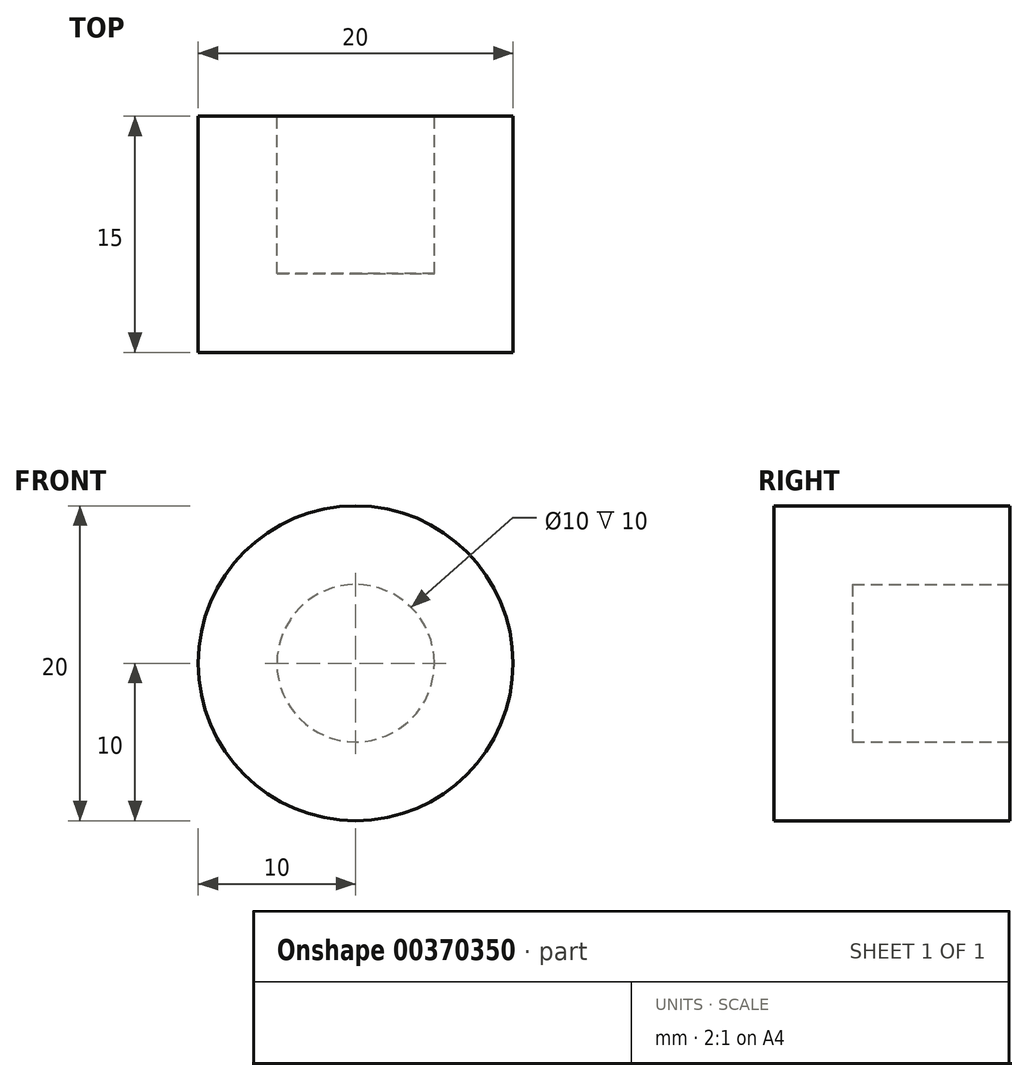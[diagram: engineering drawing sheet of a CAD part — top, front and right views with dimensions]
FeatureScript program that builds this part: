
annotation { "Feature Type Name" : "Feature", "Feature Type Description" : "" }
export const myFeature = defineFeature(function(context is Context, id is Id, definition is map)
    precondition{}
    {
        {
            var Q0;
            Q0=qCreatedBy(makeId("Right.planeOp"),FACE);
            var sketch = newSketch(context, id + "F0", { "sketchPlane" : qUnion([Q0])});
            skLineSegment(sketch, "E0", {"start": v(-10, 5) * mm, "end": v(-20, 5) * mm});
            skLineSegment(sketch, "E1", {"start": v(-20, 5) * mm, "end": v(-20, 0) * mm});
            skLineSegment(sketch, "E2", {"start": v(-20, 0) * mm, "end": v(-25, 0) * mm});
            skLineSegment(sketch, "E3", {"start": v(-25, 0) * mm, "end": v(-25, 10) * mm});
            skLineSegment(sketch, "E4", {"start": v(-25, 10) * mm, "end": v(-10, 10) * mm});
            skLineSegment(sketch, "E5", {"start": v(-10, 10) * mm, "end": v(-10, 5) * mm});
            skSolve(sketch);
        }
        {
            var Q0;
            Q0=makeQuery(id+"F0.imprint","IMPRINT",FACE,{"disambiguationData":[TD([[makeQuery(id+"F0.imprint","IMPRINT",EDGE,{"derivedFrom":sQuery(id+"F0.wireOp",EDGE,"E0")}),-1.0]])]});
            var Q1;
            Q1=sQuery(id+"F0.wireOp",EDGE,"E2");
            revolve(context, id + "F1", {"entities" : qUnion([Q0]), "axis" : qUnion([Q1]), "revolveType" : RevolveType.FULL});
        }
    });
